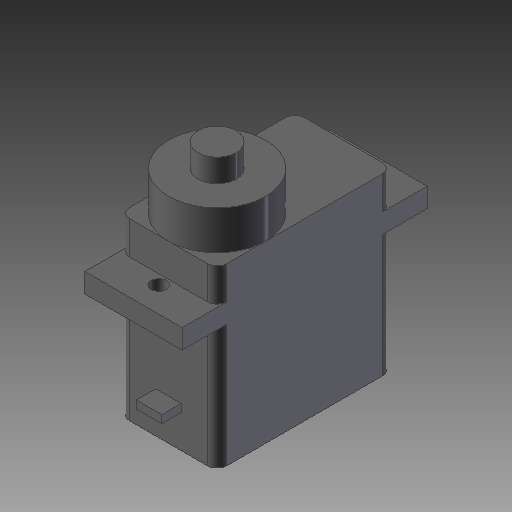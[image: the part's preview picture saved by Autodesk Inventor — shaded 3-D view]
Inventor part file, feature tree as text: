
AUTODESK INVENTOR PART (.ipt)
format: ipt  version: 2018 (Build 220112000, 112)  size: 161,792 bytes
history: native  units: in
note: dims shown in document units (in); Inventor stores cm internally (conversion verified against a paired STEP export)
features: extrude x5, sketch x5, plane x1
ambient origin geometry x8: Origin, YZ Plane, XZ Plane, XY Plane, X Axis, Y Axis, Z Axis, Center Point
bodies: Solid1 (feature_tree)
feature tree (11):
  extrude  "Extrusion1"  Depth=0.9in
  extrude  "Extrusion2"  Depth=0.9in TaperAngle=0.0deg
  plane  "Work Plane1"
  extrude  "Extrusion4"  [1 undecoded]
  extrude  "Extrusion5"  Depth=0.08in
  extrude  "Extrusion6"  Depth=0.1in TaperAngle=0.0deg
  sketch  "Sketch1"  dims[d0=0.5in d1=0.9in]
  sketch  "Sketch2"  dims[d2=0.05in d3=0.9in d4=0.0in]
  sketch  "Sketch5"  dims[d7=0.2in d8=0.0in d12=-0.17in]
  sketch  "Sketch6"  dims[d13=0.63in d14=0.08in]
  sketch  "Sketch7"  dims[d15=1.0in d16=0.1in d17=0.0in d18=0.13in d19=0.04in d20=0.17in d21=0.1in d22=0.0in d23=0.1969in d24=0.1181in d25=0.0in]
note: 1 required parameter value undecoded (feature->parameter linkage not recoverable at this tier; creation-order binding heuristic only, values carry confidence <= 0.55)
